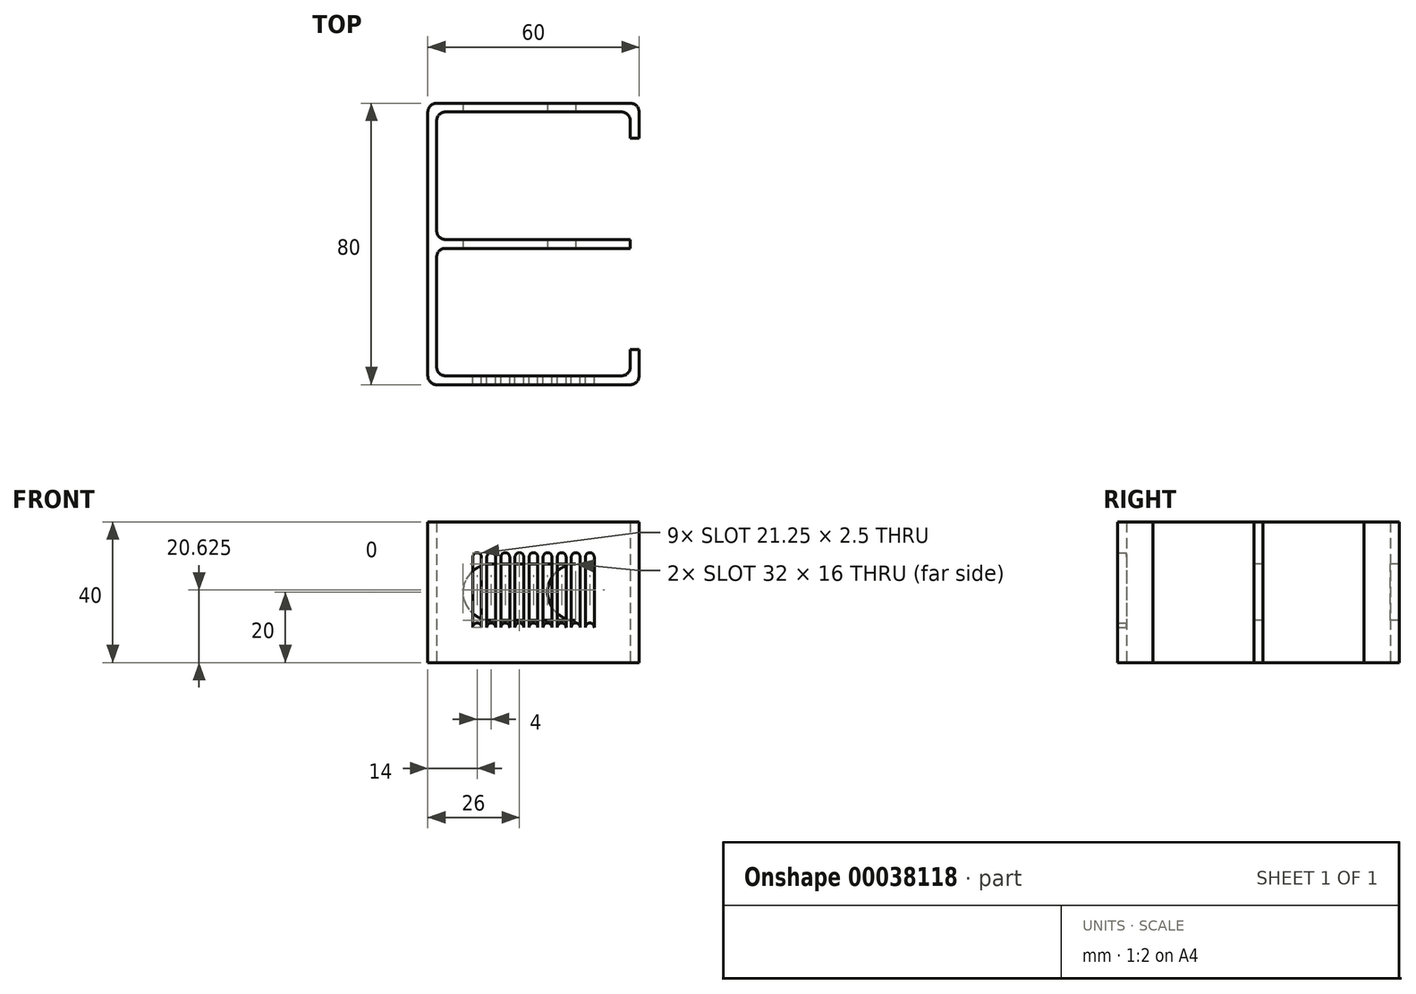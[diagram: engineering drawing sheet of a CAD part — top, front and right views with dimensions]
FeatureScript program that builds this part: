
annotation { "Feature Type Name" : "Feature", "Feature Type Description" : "" }
export const myFeature = defineFeature(function(context is Context, id is Id, definition is map)
    precondition{}
    {
        {
            assignVariable(context, id + "F0", {"name" : "WallThickness", "anyValue" : 2.5});
        }
        {
            assignVariable(context, id + "F1", {"name" : "Height", "anyValue" : 80});
        }
        {
            var Q0;
            Q0=qCreatedBy(makeId("Top.planeOp"),FACE);
            var sketch = newSketch(context, id + "F2", { "sketchPlane" : qUnion([Q0])});
            skLineSegment(sketch, "E0", {"start": v(0, 0) * mm, "end": v(60, 0) * mm});
            skLineSegment(sketch, "E1", {"start": v(2.5, 2.5) * mm, "end": v(2.5, 77.5) * mm});
            skLineSegment(sketch, "E2", {"start": v(2.5, 77.5) * mm, "end": v(57.5, 77.5) * mm});
            skLineSegment(sketch, "E3", {"start": v(57.5, 77.5) * mm, "end": v(57.5, 70) * mm});
            skLineSegment(sketch, "E4", {"start": v(57.5, 70) * mm, "end": v(60, 70) * mm});
            skLineSegment(sketch, "E5", {"start": v(60, 70) * mm, "end": v(60, 80) * mm});
            skLineSegment(sketch, "E6", {"start": v(60, 80) * mm, "end": v(0, 80) * mm});
            skLineSegment(sketch, "E7", {"start": v(0, 80) * mm, "end": v(0, 0) * mm});
            skLineSegment(sketch, "E8", {"start": v(57.5, 2.5) * mm, "end": v(2.5, 2.5) * mm});
            skLineSegment(sketch, "E9", {"start": v(2.5, 38.75) * mm, "end": v(57.5, 38.75) * mm});
            skLineSegment(sketch, "E10", {"start": v(57.5, 38.75) * mm, "end": v(57.5, 41.25) * mm});
            skLineSegment(sketch, "E11", {"start": v(57.5, 41.25) * mm, "end": v(2.5, 41.25) * mm});
            skLineSegment(sketch, "E12", {"start": v(57.5, 2.5) * mm, "end": v(57.5, 10) * mm});
            skLineSegment(sketch, "E13", {"start": v(57.5, 10) * mm, "end": v(60, 10) * mm});
            skLineSegment(sketch, "E14", {"start": v(60, 10) * mm, "end": v(60, 0) * mm});
            skLineSegment(sketch, "E15", {"start": v(-9.88, 40) * mm, "end": v(69.12, 40) * mm, "construction": true});
            skPoint(sketch, "E15.startSnap0", {"position": v(2.5, 40) * mm});
            skSolve(sketch);
        }
        {
            assignVariable(context, id + "F3", {"name" : "Width", "anyValue" : 40});
        }
        {
            var Q0;
            {var subQ1=sQuery(id+"F2.wireOp",EDGE,"E9");Q0=makeQuery(id+"F2.imprint","IMPRINT",FACE,{"disambiguationData":[TD([[makeQuery(id+"F2.imprint","IMPRINT",EDGE,{"derivedFrom":subQ1}),1.0]])]});}
            var Q1;
            Q1=makeQuery(id+"F2.imprint","IMPRINT",FACE,{"disambiguationData":[TD([[makeQuery(id+"F2.imprint","IMPRINT",EDGE,{"derivedFrom":sQuery(id+"F2.wireOp",EDGE,"E0")}),1.0]])]});
            extrude(context, id + "F4", {"entities" : qUnion([Q0, Q1]), "depth" : (getVariable(context, 'Width')) * mm});
        }
        {
            var Q0;
            Q0=makeQuery(id+"F4.opExtrude","SWEPT_FACE",FACE,{"disambiguationData":[OSD([sQuery(id+"F2.wireOp",EDGE,"E2")])]});
            var sketch = newSketch(context, id + "F5", { "sketchPlane" : qUnion([Q0])});
            skLineSegment(sketch, "E16.1", {"start": v(2.5, 40) * mm, "end": v(57.5, 40) * mm});
            skLineSegment(sketch, "E16.2", {"start": v(57.5, 40) * mm, "end": v(57.5, 0) * mm});
            skLineSegment(sketch, "E16.3", {"start": v(2.5, 0) * mm, "end": v(57.5, 0) * mm});
            skLineSegment(sketch, "E16.4", {"start": v(2.5, 40) * mm, "end": v(2.5, 0) * mm});
            skLineSegment(sketch, "E17", {"start": v(30, 40) * mm, "end": v(30, 0) * mm, "construction": true});
            skCircle(sketch, "E18", {"center": v(18, 20) * mm, "radius": 8 * mm});
            skPoint(sketch, "E18.centerSnap0", {"position": v(30, 20) * mm});
            skCircle(sketch, "E19.MirrorC", {"center": v(42, 20) * mm, "radius": 8 * mm});
            skLineSegment(sketch, "E20", {"start": v(18, 28) * mm, "end": v(42, 28) * mm});
            skLineSegment(sketch, "E21", {"start": v(42, 12) * mm, "end": v(18, 12) * mm});
            skSolve(sketch);
        }
        {
            var Q0;
            {var subQ0=sQuery(id+"F5.wireOp",EDGE,"E18");var subQ2=makeQuery(id+"F5.imprint","INTERSECT",VERTEX,{"derivedFrom":[subQ0,sQuery(id+"F5.wireOp",EDGE,"E20")]});Q0=makeQuery(id+"F5.imprint","IMPRINT",FACE,{"disambiguationData":[TD([[makeQuery(id+"F5.imprint","IMPRINT",EDGE,{"disambiguationData":[TD([[subQ2,-1.0]])],"derivedFrom":subQ0}),1.0]])]});}
            var Q1;
            {var subQ1=sQuery(id+"F5.wireOp",EDGE,"E20");Q1=makeQuery(id+"F5.imprint","IMPRINT",FACE,{"disambiguationData":[TD([[makeQuery(id+"F5.imprint","IMPRINT",EDGE,{"derivedFrom":subQ1}),-1.0]])]});}
            var Q2;
            {var subQ0=sQuery(id+"F5.wireOp",EDGE,"E19.MirrorC");var subQ2=makeQuery(id+"F5.imprint","INTERSECT",VERTEX,{"derivedFrom":[subQ0,sQuery(id+"F5.wireOp",EDGE,"E20")]});Q2=makeQuery(id+"F5.imprint","IMPRINT",FACE,{"disambiguationData":[TD([[makeQuery(id+"F5.imprint","IMPRINT",EDGE,{"disambiguationData":[TD([[subQ2,-1.0]])],"derivedFrom":subQ0}),-1.0]])]});}
            extrude(context, id + "F6", {"entities" : qUnion([Q0, Q1, Q2]), "operationType" : NewBodyOperationType.REMOVE, "endBound" : BoundingType.THROUGH_ALL, "oppositeDirection" : true, "depth" : 25 * mm, "hasSecondDirection" : true, "secondDirectionOppositeDirection" : false, "secondDirectionDepth" : (getVariable(context, 'Height') - (getVariable(context, 'WallThickness') * 2)) * mm});
        }
        {
            var Q0;
            Q0=makeQuery(id+"F4.opExtrude","SWEPT_FACE",FACE,{"disambiguationData":[OSD([sQuery(id+"F2.wireOp",EDGE,"E8")])]});
            var sketch = newSketch(context, id + "F7", { "sketchPlane" : qUnion([Q0])});
            skLineSegment(sketch, "E22.0", {"start": v(-2.5, 0) * mm, "end": v(-2.5, 0) * mm});
            skCircle(sketch, "E23", {"center": v(-30, 30) * mm, "radius": 1.25 * mm});
            skCircle(sketch, "E24.MirrorC", {"center": v(-30, 10) * mm, "radius": 1.25 * mm});
            skLineSegment(sketch, "E25", {"start": v(-28.75, 10) * mm, "end": v(-28.75, 30) * mm});
            skLineSegment(sketch, "E26", {"start": v(-31.25, 30) * mm, "end": v(-31.25, 10) * mm});
            skCircle(sketch, "E27.1.0.0", {"center": v(-26, 10) * mm, "radius": 1.25 * mm});
            skCircle(sketch, "E27.1.0.1", {"center": v(-26, 30) * mm, "radius": 1.25 * mm});
            skLineSegment(sketch, "E27.1.0.2", {"start": v(-27.25, 30) * mm, "end": v(-27.25, 10) * mm});
            skLineSegment(sketch, "E27.1.0.3", {"start": v(-24.75, 10) * mm, "end": v(-24.75, 30) * mm});
            skCircle(sketch, "E27.2.0.0", {"center": v(-22, 10) * mm, "radius": 1.25 * mm});
            skCircle(sketch, "E27.2.0.1", {"center": v(-22, 30) * mm, "radius": 1.25 * mm});
            skLineSegment(sketch, "E27.2.0.2", {"start": v(-23.25, 30) * mm, "end": v(-23.25, 10) * mm});
            skLineSegment(sketch, "E27.2.0.3", {"start": v(-20.75, 10) * mm, "end": v(-20.75, 30) * mm});
            skCircle(sketch, "E27.3.0.0", {"center": v(-18, 10) * mm, "radius": 1.25 * mm});
            skCircle(sketch, "E27.3.0.1", {"center": v(-18, 30) * mm, "radius": 1.25 * mm});
            skLineSegment(sketch, "E27.3.0.2", {"start": v(-19.25, 30) * mm, "end": v(-19.25, 10) * mm});
            skLineSegment(sketch, "E27.3.0.3", {"start": v(-16.75, 10) * mm, "end": v(-16.75, 30) * mm});
            skLineSegment(sketch, "E27.direction1", {"start": v(-30, 10) * mm, "end": v(-26, 10) * mm, "construction": true});
            skLineSegment(sketch, "E28.1.0.0", {"start": v(-35.25, 30) * mm, "end": v(-35.25, 10) * mm});
            skLineSegment(sketch, "E28.1.0.1", {"start": v(-32.75, 10) * mm, "end": v(-32.75, 30) * mm});
            skCircle(sketch, "E28.1.0.2", {"center": v(-34, 10) * mm, "radius": 1.25 * mm});
            skCircle(sketch, "E28.1.0.3", {"center": v(-34, 30) * mm, "radius": 1.25 * mm});
            skLineSegment(sketch, "E28.2.0.0", {"start": v(-39.25, 30) * mm, "end": v(-39.25, 10) * mm});
            skLineSegment(sketch, "E28.2.0.1", {"start": v(-36.75, 10) * mm, "end": v(-36.75, 30) * mm});
            skCircle(sketch, "E28.2.0.2", {"center": v(-38, 10) * mm, "radius": 1.25 * mm});
            skCircle(sketch, "E28.2.0.3", {"center": v(-38, 30) * mm, "radius": 1.25 * mm});
            skLineSegment(sketch, "E28.3.0.0", {"start": v(-43.25, 30) * mm, "end": v(-43.25, 10) * mm});
            skLineSegment(sketch, "E28.3.0.1", {"start": v(-40.75, 10) * mm, "end": v(-40.75, 30) * mm});
            skCircle(sketch, "E28.3.0.2", {"center": v(-42, 10) * mm, "radius": 1.25 * mm});
            skCircle(sketch, "E28.3.0.3", {"center": v(-42, 30) * mm, "radius": 1.25 * mm});
            skLineSegment(sketch, "E28.direction1", {"start": v(-31.25, 10) * mm, "end": v(-35.25, 10) * mm, "construction": true});
            skLineSegment(sketch, "E29.0.0", {"start": v(-2.5, 0) * mm, "end": v(-60, 0) * mm});
            skLineSegment(sketch, "E29.0.1", {"start": v(-60, 0) * mm, "end": v(-60, 40) * mm});
            skLineSegment(sketch, "E29.0.2", {"start": v(-60, 40) * mm, "end": v(0, 40) * mm});
            skLineSegment(sketch, "E29.0.3", {"start": v(0, 40) * mm, "end": v(0, 0) * mm});
            skLineSegment(sketch, "E30", {"start": v(-30, 46.57) * mm, "end": v(-30, -8.07) * mm, "construction": true});
            skPoint(sketch, "E30.startSnap0", {"position": v(-30, 40) * mm});
            skCircle(sketch, "E31.0.4.0", {"center": v(-14, 10) * mm, "radius": 1.25 * mm});
            skCircle(sketch, "E31.2.4.0", {"center": v(-14, 30) * mm, "radius": 1.25 * mm});
            skLineSegment(sketch, "E31.4.4.0", {"start": v(-15.25, 30) * mm, "end": v(-15.25, 10) * mm});
            skLineSegment(sketch, "E31.7.4.0", {"start": v(-12.75, 10) * mm, "end": v(-12.75, 30) * mm});
            skLineSegment(sketch, "E32.0.4.0", {"start": v(-47.25, 30) * mm, "end": v(-47.25, 10) * mm});
            skLineSegment(sketch, "E32.3.4.0", {"start": v(-44.75, 10) * mm, "end": v(-44.75, 30) * mm});
            skCircle(sketch, "E32.6.4.0", {"center": v(-46, 10) * mm, "radius": 1.25 * mm});
            skCircle(sketch, "E32.8.4.0", {"center": v(-46, 30) * mm, "radius": 1.25 * mm});
            skSolve(sketch);
        }
        {
            var Q0;
            {var subQ0=sQuery(id+"F7.wireOp",EDGE,"E31.2.4.0");var subQ2=makeQuery(id+"F7.imprint","INTERSECT",VERTEX,{"derivedFrom":[subQ0,sQuery(id+"F7.wireOp",EDGE,"E31.4.4.0")]});Q0=makeQuery(id+"F7.imprint","IMPRINT",FACE,{"disambiguationData":[TD([[makeQuery(id+"F7.imprint","IMPRINT",EDGE,{"disambiguationData":[TD([[subQ2,1.0]])],"derivedFrom":subQ0}),1.0]])]});}
            var Q1;
            {var subQ0=sQuery(id+"F7.wireOp",EDGE,"E31.4.4.0");Q1=makeQuery(id+"F7.imprint","IMPRINT",FACE,{"disambiguationData":[TD([[makeQuery(id+"F7.imprint","IMPRINT",EDGE,{"derivedFrom":subQ0}),1.0]])]});}
            var Q2;
            {var subQ0=sQuery(id+"F7.wireOp",EDGE,"E31.0.4.0");var subQ2=makeQuery(id+"F7.imprint","INTERSECT",VERTEX,{"derivedFrom":[subQ0,sQuery(id+"F7.wireOp",EDGE,"E31.4.4.0")]});Q2=makeQuery(id+"F7.imprint","IMPRINT",FACE,{"disambiguationData":[TD([[makeQuery(id+"F7.imprint","IMPRINT",EDGE,{"disambiguationData":[TD([[subQ2,1.0]])],"derivedFrom":subQ0}),-1.0]])]});}
            var Q3;
            {var subQ0=sQuery(id+"F7.wireOp",EDGE,"E27.3.0.0");var subQ2=makeQuery(id+"F7.imprint","INTERSECT",VERTEX,{"derivedFrom":[subQ0,sQuery(id+"F7.wireOp",EDGE,"E27.3.0.2")]});Q3=makeQuery(id+"F7.imprint","IMPRINT",FACE,{"disambiguationData":[TD([[makeQuery(id+"F7.imprint","IMPRINT",EDGE,{"disambiguationData":[TD([[subQ2,1.0]])],"derivedFrom":subQ0}),-1.0]])]});}
            var Q4;
            {var subQ1=sQuery(id+"F7.wireOp",EDGE,"E27.3.0.2");Q4=makeQuery(id+"F7.imprint","IMPRINT",FACE,{"disambiguationData":[TD([[makeQuery(id+"F7.imprint","IMPRINT",EDGE,{"derivedFrom":subQ1}),1.0]])]});}
            var Q5;
            {var subQ0=sQuery(id+"F7.wireOp",EDGE,"E27.3.0.1");var subQ2=makeQuery(id+"F7.imprint","INTERSECT",VERTEX,{"derivedFrom":[subQ0,sQuery(id+"F7.wireOp",EDGE,"E27.3.0.2")]});Q5=makeQuery(id+"F7.imprint","IMPRINT",FACE,{"disambiguationData":[TD([[makeQuery(id+"F7.imprint","IMPRINT",EDGE,{"disambiguationData":[TD([[subQ2,1.0]])],"derivedFrom":subQ0}),1.0]])]});}
            var Q6;
            {var subQ0=sQuery(id+"F7.wireOp",EDGE,"E27.2.0.1");var subQ2=makeQuery(id+"F7.imprint","INTERSECT",VERTEX,{"derivedFrom":[subQ0,sQuery(id+"F7.wireOp",EDGE,"E27.2.0.2")]});Q6=makeQuery(id+"F7.imprint","IMPRINT",FACE,{"disambiguationData":[TD([[makeQuery(id+"F7.imprint","IMPRINT",EDGE,{"disambiguationData":[TD([[subQ2,1.0]])],"derivedFrom":subQ0}),1.0]])]});}
            var Q7;
            {var subQ1=sQuery(id+"F7.wireOp",EDGE,"E27.2.0.2");Q7=makeQuery(id+"F7.imprint","IMPRINT",FACE,{"disambiguationData":[TD([[makeQuery(id+"F7.imprint","IMPRINT",EDGE,{"derivedFrom":subQ1}),1.0]])]});}
            var Q8;
            {var subQ0=sQuery(id+"F7.wireOp",EDGE,"E27.2.0.0");var subQ2=makeQuery(id+"F7.imprint","INTERSECT",VERTEX,{"derivedFrom":[subQ0,sQuery(id+"F7.wireOp",EDGE,"E27.2.0.2")]});Q8=makeQuery(id+"F7.imprint","IMPRINT",FACE,{"disambiguationData":[TD([[makeQuery(id+"F7.imprint","IMPRINT",EDGE,{"disambiguationData":[TD([[subQ2,1.0]])],"derivedFrom":subQ0}),-1.0]])]});}
            var Q9;
            {var subQ0=sQuery(id+"F7.wireOp",EDGE,"E27.1.0.0");var subQ2=makeQuery(id+"F7.imprint","INTERSECT",VERTEX,{"derivedFrom":[subQ0,sQuery(id+"F7.wireOp",EDGE,"E27.1.0.2")]});Q9=makeQuery(id+"F7.imprint","IMPRINT",FACE,{"disambiguationData":[TD([[makeQuery(id+"F7.imprint","IMPRINT",EDGE,{"disambiguationData":[TD([[subQ2,1.0]])],"derivedFrom":subQ0}),-1.0]])]});}
            var Q10;
            {var subQ0=sQuery(id+"F7.wireOp",EDGE,"E27.1.0.1");var subQ2=makeQuery(id+"F7.imprint","INTERSECT",VERTEX,{"derivedFrom":[subQ0,sQuery(id+"F7.wireOp",EDGE,"E27.1.0.2")]});Q10=makeQuery(id+"F7.imprint","IMPRINT",FACE,{"disambiguationData":[TD([[makeQuery(id+"F7.imprint","IMPRINT",EDGE,{"disambiguationData":[TD([[subQ2,1.0]])],"derivedFrom":subQ0}),1.0]])]});}
            var Q11;
            {var subQ0=sQuery(id+"F7.wireOp",EDGE,"E23");var subQ2=makeQuery(id+"F7.imprint","INTERSECT",VERTEX,{"derivedFrom":[subQ0,sQuery(id+"F7.wireOp",EDGE,"E25")]});Q11=makeQuery(id+"F7.imprint","IMPRINT",FACE,{"disambiguationData":[TD([[makeQuery(id+"F7.imprint","IMPRINT",EDGE,{"disambiguationData":[TD([[subQ2,-1.0]])],"derivedFrom":subQ0}),1.0]])]});}
            var Q12;
            {var subQ0=sQuery(id+"F7.wireOp",EDGE,"E25");Q12=makeQuery(id+"F7.imprint","IMPRINT",FACE,{"disambiguationData":[TD([[makeQuery(id+"F7.imprint","IMPRINT",EDGE,{"derivedFrom":subQ0}),1.0]])]});}
            var Q13;
            {var subQ0=sQuery(id+"F7.wireOp",EDGE,"E24.MirrorC");var subQ2=makeQuery(id+"F7.imprint","INTERSECT",VERTEX,{"derivedFrom":[subQ0,sQuery(id+"F7.wireOp",EDGE,"E25")]});Q13=makeQuery(id+"F7.imprint","IMPRINT",FACE,{"disambiguationData":[TD([[makeQuery(id+"F7.imprint","IMPRINT",EDGE,{"disambiguationData":[TD([[subQ2,-1.0]])],"derivedFrom":subQ0}),-1.0]])]});}
            var Q14;
            {var subQ0=sQuery(id+"F7.wireOp",EDGE,"E27.1.0.2");Q14=makeQuery(id+"F7.imprint","IMPRINT",FACE,{"disambiguationData":[TD([[makeQuery(id+"F7.imprint","IMPRINT",EDGE,{"derivedFrom":subQ0}),1.0]])]});}
            var Q15;
            {var subQ0=sQuery(id+"F7.wireOp",EDGE,"E28.1.0.2");var subQ2=makeQuery(id+"F7.imprint","INTERSECT",VERTEX,{"derivedFrom":[sQuery(id+"F7.wireOp",EDGE,"E28.1.0.0"),subQ0]});Q15=makeQuery(id+"F7.imprint","IMPRINT",FACE,{"disambiguationData":[TD([[makeQuery(id+"F7.imprint","IMPRINT",EDGE,{"disambiguationData":[TD([[subQ2,1.0]])],"derivedFrom":subQ0}),-1.0]])]});}
            var Q16;
            {var subQ2=sQuery(id+"F7.wireOp",EDGE,"E28.1.0.0");Q16=makeQuery(id+"F7.imprint","IMPRINT",FACE,{"disambiguationData":[TD([[makeQuery(id+"F7.imprint","IMPRINT",EDGE,{"derivedFrom":subQ2}),1.0]])]});}
            var Q17;
            {var subQ0=sQuery(id+"F7.wireOp",EDGE,"E28.1.0.3");var subQ2=makeQuery(id+"F7.imprint","INTERSECT",VERTEX,{"derivedFrom":[sQuery(id+"F7.wireOp",EDGE,"E28.1.0.0"),subQ0]});Q17=makeQuery(id+"F7.imprint","IMPRINT",FACE,{"disambiguationData":[TD([[makeQuery(id+"F7.imprint","IMPRINT",EDGE,{"disambiguationData":[TD([[subQ2,1.0]])],"derivedFrom":subQ0}),1.0]])]});}
            var Q18;
            {var subQ0=sQuery(id+"F7.wireOp",EDGE,"E28.2.0.3");var subQ2=makeQuery(id+"F7.imprint","INTERSECT",VERTEX,{"derivedFrom":[sQuery(id+"F7.wireOp",EDGE,"E28.2.0.0"),subQ0]});Q18=makeQuery(id+"F7.imprint","IMPRINT",FACE,{"disambiguationData":[TD([[makeQuery(id+"F7.imprint","IMPRINT",EDGE,{"disambiguationData":[TD([[subQ2,1.0]])],"derivedFrom":subQ0}),1.0]])]});}
            var Q19;
            {var subQ2=sQuery(id+"F7.wireOp",EDGE,"E28.2.0.0");Q19=makeQuery(id+"F7.imprint","IMPRINT",FACE,{"disambiguationData":[TD([[makeQuery(id+"F7.imprint","IMPRINT",EDGE,{"derivedFrom":subQ2}),1.0]])]});}
            var Q20;
            {var subQ0=sQuery(id+"F7.wireOp",EDGE,"E28.2.0.2");var subQ2=makeQuery(id+"F7.imprint","INTERSECT",VERTEX,{"derivedFrom":[sQuery(id+"F7.wireOp",EDGE,"E28.2.0.0"),subQ0]});Q20=makeQuery(id+"F7.imprint","IMPRINT",FACE,{"disambiguationData":[TD([[makeQuery(id+"F7.imprint","IMPRINT",EDGE,{"disambiguationData":[TD([[subQ2,1.0]])],"derivedFrom":subQ0}),-1.0]])]});}
            var Q21;
            {var subQ0=sQuery(id+"F7.wireOp",EDGE,"E28.3.0.2");var subQ2=makeQuery(id+"F7.imprint","INTERSECT",VERTEX,{"derivedFrom":[sQuery(id+"F7.wireOp",EDGE,"E28.3.0.0"),subQ0]});Q21=makeQuery(id+"F7.imprint","IMPRINT",FACE,{"disambiguationData":[TD([[makeQuery(id+"F7.imprint","IMPRINT",EDGE,{"disambiguationData":[TD([[subQ2,1.0]])],"derivedFrom":subQ0}),-1.0]])]});}
            var Q22;
            {var subQ2=sQuery(id+"F7.wireOp",EDGE,"E28.3.0.0");Q22=makeQuery(id+"F7.imprint","IMPRINT",FACE,{"disambiguationData":[TD([[makeQuery(id+"F7.imprint","IMPRINT",EDGE,{"derivedFrom":subQ2}),1.0]])]});}
            var Q23;
            {var subQ0=sQuery(id+"F7.wireOp",EDGE,"E28.3.0.3");var subQ2=makeQuery(id+"F7.imprint","INTERSECT",VERTEX,{"derivedFrom":[sQuery(id+"F7.wireOp",EDGE,"E28.3.0.0"),subQ0]});Q23=makeQuery(id+"F7.imprint","IMPRINT",FACE,{"disambiguationData":[TD([[makeQuery(id+"F7.imprint","IMPRINT",EDGE,{"disambiguationData":[TD([[subQ2,1.0]])],"derivedFrom":subQ0}),1.0]])]});}
            var Q24;
            {var subQ0=sQuery(id+"F7.wireOp",EDGE,"E32.8.4.0");var subQ2=makeQuery(id+"F7.imprint","INTERSECT",VERTEX,{"derivedFrom":[sQuery(id+"F7.wireOp",EDGE,"E32.0.4.0"),subQ0]});Q24=makeQuery(id+"F7.imprint","IMPRINT",FACE,{"disambiguationData":[TD([[makeQuery(id+"F7.imprint","IMPRINT",EDGE,{"disambiguationData":[TD([[subQ2,1.0]])],"derivedFrom":subQ0}),1.0]])]});}
            var Q25;
            {var subQ2=sQuery(id+"F7.wireOp",EDGE,"E32.0.4.0");Q25=makeQuery(id+"F7.imprint","IMPRINT",FACE,{"disambiguationData":[TD([[makeQuery(id+"F7.imprint","IMPRINT",EDGE,{"derivedFrom":subQ2}),1.0]])]});}
            var Q26;
            {var subQ0=sQuery(id+"F7.wireOp",EDGE,"E32.6.4.0");var subQ2=makeQuery(id+"F7.imprint","INTERSECT",VERTEX,{"derivedFrom":[sQuery(id+"F7.wireOp",EDGE,"E32.0.4.0"),subQ0]});Q26=makeQuery(id+"F7.imprint","IMPRINT",FACE,{"disambiguationData":[TD([[makeQuery(id+"F7.imprint","IMPRINT",EDGE,{"disambiguationData":[TD([[subQ2,1.0]])],"derivedFrom":subQ0}),-1.0]])]});}
            extrude(context, id + "F8", {"entities" : qUnion([Q0, Q1, Q2, Q3, Q4, Q5, Q6, Q7, Q8, Q9, Q10, Q11, Q12, Q13, Q14, Q15, Q16, Q17, Q18, Q19, Q20, Q21, Q22, Q23, Q24, Q25, Q26]), "operationType" : NewBodyOperationType.REMOVE, "endBound" : BoundingType.THROUGH_ALL, "oppositeDirection" : true, "depth" : 25 * mm});
        }
        {
            var Q0;
            Q0=makeQuery(id+"F4.opExtrude","SWEPT_EDGE",EDGE,{"disambiguationData":[OSD([sQuery(id+"F2.wireOp",EDGE,"3472fc9f-d063-4f2d-9264-32a1147505e8"),sQuery(id+"F2.wireOp",EDGE,"E0")])]});
            var Q1;
            Q1=makeQuery(id+"F4.opExtrude","SWEPT_EDGE",EDGE,{"disambiguationData":[OSD([sQuery(id+"F2.wireOp",EDGE,"E8"),sQuery(id+"F2.wireOp",EDGE,"9d5fafd8-8bf5-4d6b-83b4-35ccdc5cc1bc")])]});
            var Q2;
            Q2=makeQuery(id+"F4.opExtrude","SWEPT_EDGE",EDGE,{"disambiguationData":[OSD([sQuery(id+"F2.wireOp",EDGE,"E0"),sQuery(id+"F2.wireOp",EDGE,"E1")])]});
            var Q3;
            Q3=makeQuery(id+"F4.opExtrude","SWEPT_EDGE",EDGE,{"disambiguationData":[OSD([sQuery(id+"F2.wireOp",EDGE,"E7"),sQuery(id+"F2.wireOp",EDGE,"E8")])]});
            var Q4;
            Q4=makeQuery(id+"F4.opExtrude","SWEPT_EDGE",EDGE,{"disambiguationData":[OSD([sQuery(id+"F2.wireOp",EDGE,"E1"),sQuery(id+"F2.wireOp",EDGE,"E2")])]});
            var Q5;
            Q5=makeQuery(id+"F4.opExtrude","SWEPT_EDGE",EDGE,{"disambiguationData":[OSD([sQuery(id+"F2.wireOp",EDGE,"E5"),sQuery(id+"F2.wireOp",EDGE,"E6")])]});
            var Q6;
            Q6=makeQuery(id+"F4.opExtrude","SWEPT_EDGE",EDGE,{"disambiguationData":[OSD([sQuery(id+"F2.wireOp",EDGE,"E2"),sQuery(id+"F2.wireOp",EDGE,"E3")])]});
            var Q7;
            Q7=makeQuery(id+"F4.opExtrude","SWEPT_EDGE",EDGE,{"disambiguationData":[OSD([sQuery(id+"F2.wireOp",EDGE,"E6"),sQuery(id+"F2.wireOp",EDGE,"E7")])]});
            fillet(context, id + "F9", {"entities" : qUnion([Q0, Q1, Q2, Q3, Q4, Q5, Q6, Q7]), "radius" : (getVariable(context, 'WallThickness')) * mm, "tangentPropagation" : true, "allowEdgeOverflow" : false});
        }
    });
